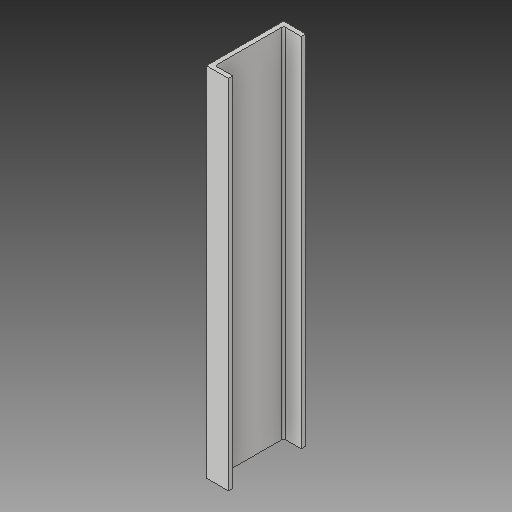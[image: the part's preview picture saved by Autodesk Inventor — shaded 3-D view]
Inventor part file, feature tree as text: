
AUTODESK INVENTOR PART (.ipt)
format: ipt  version: 2019 (Build 230136000, 136)  size: 106,496 bytes
history: native  units: in
note: dims shown in document units (in); Inventor stores cm internally (conversion verified against a paired STEP export)
features: other x3, sketch x3
ambient origin geometry x8: Origin, YZ Plane, XZ Plane, XY Plane, X Axis, Y Axis, Z Axis, Center Point
bodies: Solid1 (feature_tree)
feature tree (6):
  other  "Base1.ipt"
  other  "Solid1::Base1.ipt"
  other  "TaggingFeature1"
  sketch  "Sketch1"  dims[d0=0.3937in]
  sketch  "Sketch2"
  sketch  "Sketch3"
